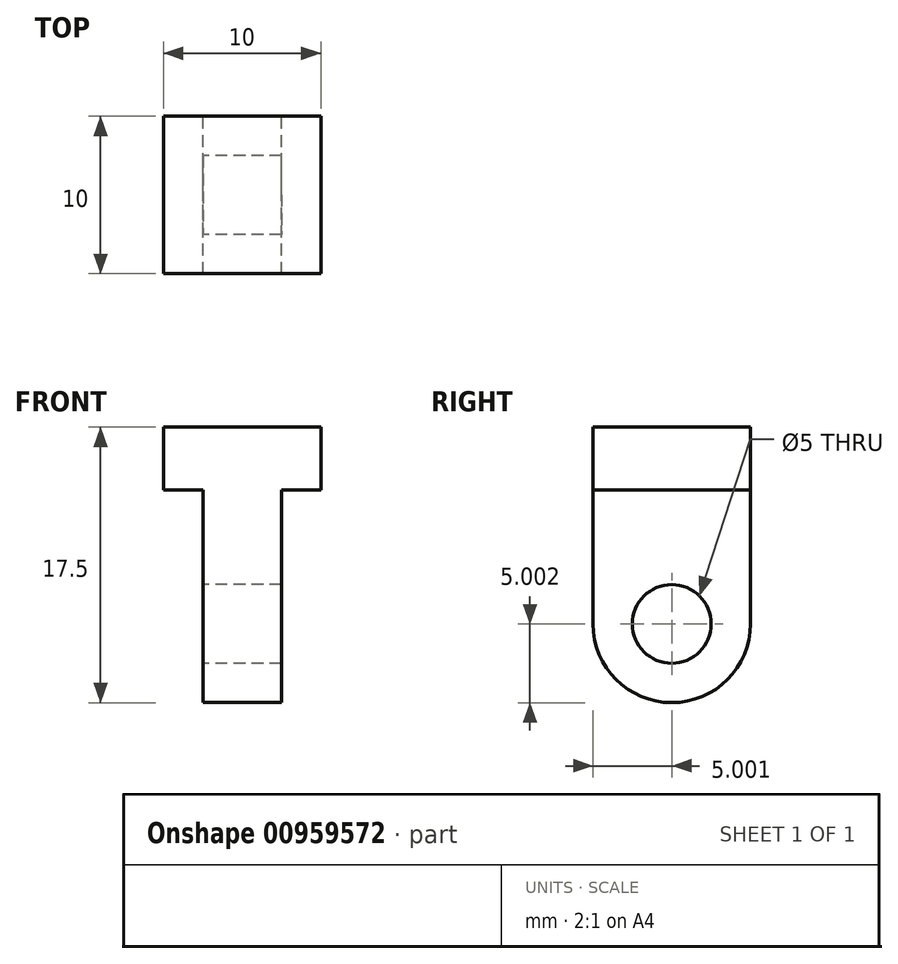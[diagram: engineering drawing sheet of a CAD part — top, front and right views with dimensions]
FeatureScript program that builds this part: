
annotation { "Feature Type Name" : "Feature", "Feature Type Description" : "" }
export const myFeature = defineFeature(function(context is Context, id is Id, definition is map)
    precondition{}
    {
        {
            var Q0;
            Q0=qCreatedBy(makeId("Right.planeOp"),FACE);
            var sketch = newSketch(context, id + "F0", { "sketchPlane" : qUnion([Q0])});
            skArc(sketch, "E0", {"start": v(-57.23, 37.75) * mm, "mid": v(-52.23, 32.75) * mm, "end": v(-47.23, 37.75) * mm});
            skLineSegment(sketch, "E1", {"start": v(-47.23, 37.75) * mm, "end": v(-47.23, 42.75) * mm});
            skLineSegment(sketch, "E2", {"start": v(-57.23, 37.75) * mm, "end": v(-57.23, 42.75) * mm});
            skLineSegment(sketch, "E3", {"start": v(-57.23, 42.75) * mm, "end": v(-47.23, 42.75) * mm});
            skSolve(sketch);
        }
        {
            var Q0;
            Q0=makeQuery(id+"F0.imprint","IMPRINT",FACE,{"disambiguationData":[TD([[makeQuery(id+"F0.imprint","IMPRINT",EDGE,{"derivedFrom":sQuery(id+"F0.wireOp",EDGE,"E0")}),1.0]])]});
            extrude(context, id + "F1", {"entities" : qUnion([Q0]), "depth" : 5 * mm, "offsetDistance" : 25 * mm});
        }
        {
            var Q0;
            Q0=makeQuery(id+"F1.opExtrude","CAP_FACE",FACE,{"disambiguationData":[OSD([sQuery(id+"F0.wireOp",EDGE,"E0"),sQuery(id+"F0.wireOp",EDGE,"E1"),sQuery(id+"F0.wireOp",EDGE,"E2"),sQuery(id+"F0.wireOp",EDGE,"E3")])],"isStart":true});
            var sketch = newSketch(context, id + "F2", { "sketchPlane" : qUnion([Q0])});
            skLineSegment(sketch, "E4", {"start": v(52.23, 42.75) * mm, "end": v(52.23, 32.75) * mm});
            skLineSegment(sketch, "E5", {"start": v(47.23, 37.75) * mm, "end": v(57.23, 37.75) * mm});
            skPoint(sketch, "E6", {"position": v(52.23, 37.75) * mm});
            skSolve(sketch);
        }
        {
            var Q0;
            Q0=sQuery(id+"F2.wireOp",VERTEX,"E6");
            var Q1;
            Q1=makeQuery(id+"F1.opExtrude","SWEPT_BODY",BODY,{"disambiguationData":[OSD([sQuery(id+"F0.wireOp",EDGE,"E0"),sQuery(id+"F0.wireOp",EDGE,"E1"),sQuery(id+"F0.wireOp",EDGE,"E2"),sQuery(id+"F0.wireOp",EDGE,"E3")])]});
            hole(context, id + "F3", {"style" : HoleStyle.SIMPLE, "endStyle" : HoleEndStyle.THROUGH, "holeDiameter" : 5 * mm, "majorDiameter" : 5 * mm, "isTappedThrough" : true, "tappedDepth" : 12 * mm, "tapClearance" : 3, "locations" : qUnion([Q0]), "scope" : qUnion([Q1])});
        }
        {
            var Q0;
            Q0=makeQuery(id+"F1.opExtrude","SWEPT_FACE",FACE,{"disambiguationData":[OSD([sQuery(id+"F0.wireOp",EDGE,"E3")])]});
            extrude(context, id + "F4", {"entities" : qUnion([Q0]), "operationType" : NewBodyOperationType.ADD, "depth" : 7.5 * mm, "offsetDistance" : 25 * mm});
        }
        {
            var Q0;
            {var subQ0=sQuery(id+"F0.wireOp",EDGE,"E3");Q0=makeQuery(id+"F4.boolean.opBoolean","MERGE",FACE,{"derivedFrom":[makeQuery(id+"F1.opExtrude","CAP_FACE",FACE,{"disambiguationData":[OSD([sQuery(id+"F0.wireOp",EDGE,"E0"),sQuery(id+"F0.wireOp",EDGE,"E1"),sQuery(id+"F0.wireOp",EDGE,"E2"),subQ0])],"isStart":true}),makeQuery(id+"F4.opExtrude","SWEPT_FACE",FACE,{"disambiguationData":[OSD([subQ0]),TDD([makeQuery(id+"F1.opExtrude","CAP_EDGE",EDGE,{"disambiguationData":[OSD([subQ0])],"isStart":true})])]})]});}
            var sketch = newSketch(context, id + "F5", { "sketchPlane" : qUnion([Q0])});
            skLineSegment(sketch, "E7", {"start": v(57.23, 50.25) * mm, "end": v(57.23, 46.25) * mm});
            skLineSegment(sketch, "E8", {"start": v(57.23, 46.25) * mm, "end": v(47.23, 46.25) * mm});
            skLineSegment(sketch, "E9", {"start": v(47.23, 46.25) * mm, "end": v(47.23, 50.25) * mm});
            skLineSegment(sketch, "E10", {"start": v(47.23, 50.25) * mm, "end": v(57.23, 50.25) * mm});
            skSolve(sketch);
        }
        {
            var Q0;
            Q0=makeQuery(id+"F5.imprint","IMPRINT",FACE,{"disambiguationData":[TD([[makeQuery(id+"F5.imprint","IMPRINT",EDGE,{"derivedFrom":sQuery(id+"F5.wireOp",EDGE,"E7")}),1.0]])]});
            extrude(context, id + "F6", {"entities" : qUnion([Q0]), "operationType" : NewBodyOperationType.ADD, "depth" : 2.5 * mm, "offsetDistance" : 25 * mm});
        }
        {
            var Q0;
            {var subQ0=sQuery(id+"F0.wireOp",EDGE,"E3");Q0=makeQuery(id+"F4.boolean.opBoolean","MERGE",FACE,{"derivedFrom":[makeQuery(id+"F1.opExtrude","CAP_FACE",FACE,{"disambiguationData":[OSD([sQuery(id+"F0.wireOp",EDGE,"E0"),sQuery(id+"F0.wireOp",EDGE,"E1"),sQuery(id+"F0.wireOp",EDGE,"E2"),subQ0])],"isStart":false}),makeQuery(id+"F4.opExtrude","SWEPT_FACE",FACE,{"disambiguationData":[OSD([subQ0]),TDD([makeQuery(id+"F1.opExtrude","CAP_EDGE",EDGE,{"disambiguationData":[OSD([subQ0])],"isStart":false})])]})]});}
            var sketch = newSketch(context, id + "F7", { "sketchPlane" : qUnion([Q0])});
            skLineSegment(sketch, "E11", {"start": v(-57.23, 50.25) * mm, "end": v(-57.23, 46.25) * mm});
            skLineSegment(sketch, "E12", {"start": v(-57.23, 46.25) * mm, "end": v(-47.23, 46.25) * mm});
            skLineSegment(sketch, "E13", {"start": v(-47.23, 46.25) * mm, "end": v(-47.23, 50.25) * mm});
            skLineSegment(sketch, "E14", {"start": v(-47.23, 50.25) * mm, "end": v(-57.23, 50.25) * mm});
            skSolve(sketch);
        }
        {
            var Q0;
            Q0=makeQuery(id+"F7.imprint","IMPRINT",FACE,{"disambiguationData":[TD([[makeQuery(id+"F7.imprint","IMPRINT",EDGE,{"derivedFrom":sQuery(id+"F7.wireOp",EDGE,"E11")}),-1.0]])]});
            extrude(context, id + "F8", {"entities" : qUnion([Q0]), "operationType" : NewBodyOperationType.ADD, "depth" : 2.5 * mm, "offsetDistance" : 25 * mm});
        }
    });
